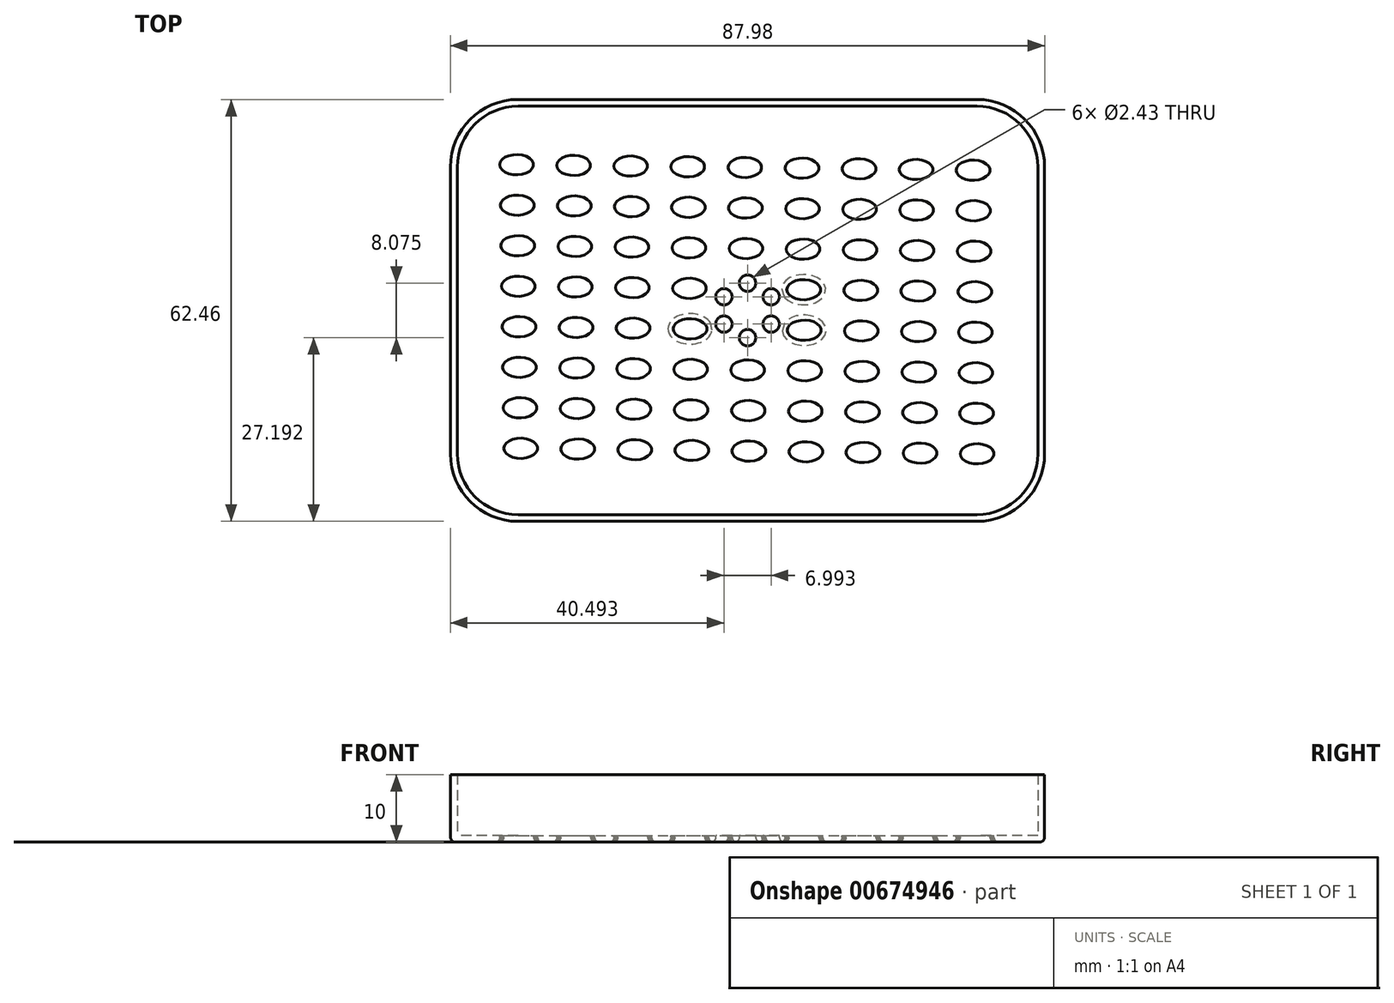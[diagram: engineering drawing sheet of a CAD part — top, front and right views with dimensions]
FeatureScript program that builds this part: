
annotation { "Feature Type Name" : "Feature", "Feature Type Description" : "" }
export const myFeature = defineFeature(function(context is Context, id is Id, definition is map)
    precondition{}
    {
        {
            var Q0;
            Q0=qCreatedBy(makeId("Top.planeOp"),FACE);
            var sketch = newSketch(context, id + "F0", { "sketchPlane" : qUnion([Q0])});
            skLineSegment(sketch, "E0.bottom", {"start": v(-33.99, 31.23) * mm, "end": v(33.99, 31.23) * mm});
            skLineSegment(sketch, "E0.top", {"start": v(-33.99, -31.23) * mm, "end": v(33.99, -31.23) * mm});
            skLineSegment(sketch, "E0.left", {"start": v(-43.99, 21.23) * mm, "end": v(-43.99, -21.23) * mm});
            skLineSegment(sketch, "E0.right", {"start": v(43.99, 21.23) * mm, "end": v(43.99, -21.23) * mm});
            skPoint(sketch, "E0.middle", {"position": v(0, 0) * mm});
            skPoint(sketch, "E1.visualSharp", {"position": v(-43.99, 31.23) * mm});
            skArc(sketch, "E1.filletArc", {"start": v(-33.99, 31.23) * mm, "mid": v(-41.06, 28.3) * mm, "end": v(-43.99, 21.23) * mm});
            skPoint(sketch, "E2.visualSharp", {"position": v(43.99, 31.23) * mm});
            skArc(sketch, "E2.filletArc", {"start": v(43.99, 21.23) * mm, "mid": v(41.06, 28.3) * mm, "end": v(33.99, 31.23) * mm});
            skPoint(sketch, "E3.visualSharp", {"position": v(43.99, -31.23) * mm});
            skArc(sketch, "E3.filletArc", {"start": v(33.99, -31.23) * mm, "mid": v(41.06, -28.3) * mm, "end": v(43.99, -21.23) * mm});
            skPoint(sketch, "E4.visualSharp", {"position": v(-43.99, -31.23) * mm});
            skArc(sketch, "E4.filletArc", {"start": v(-43.99, -21.23) * mm, "mid": v(-41.06, -28.3) * mm, "end": v(-33.99, -31.23) * mm});
            skSolve(sketch);
        }
        {
            var Q0;
            Q0 = qSketchRegion(id + "F0", true);
            extrude(context, id + "F1", {"entities" : qUnion([Q0]), "depth" : 10 * mm, "offsetDistance" : 25 * mm});
        }
        {
            var Q0;
            Q0=makeQuery(id+"F1.opExtrude","CAP_FACE",FACE,{"disambiguationData":[OSD([sQuery(id+"F0.wireOp",EDGE,"E0.bottom"),sQuery(id+"F0.wireOp",EDGE,"E0.top"),sQuery(id+"F0.wireOp",EDGE,"E0.left"),sQuery(id+"F0.wireOp",EDGE,"E0.right"),sQuery(id+"F0.wireOp",EDGE,"E1.filletArc"),sQuery(id+"F0.wireOp",EDGE,"E2.filletArc"),sQuery(id+"F0.wireOp",EDGE,"E3.filletArc"),sQuery(id+"F0.wireOp",EDGE,"E4.filletArc")])],"isStart":false});
            shell(context, id + "F2", {"entities" : qUnion([Q0]), "thickness" : 1 * mm});
        }
        {
            var Q0;
            Q0=makeQuery(id+"F2.opShell","OFFSET_FACE",FACE,{"disambiguationData":[OSD([sQuery(id+"F0.wireOp",EDGE,"E0.bottom"),sQuery(id+"F0.wireOp",EDGE,"E0.top"),sQuery(id+"F0.wireOp",EDGE,"E0.left"),sQuery(id+"F0.wireOp",EDGE,"E0.right"),sQuery(id+"F0.wireOp",EDGE,"E1.filletArc"),sQuery(id+"F0.wireOp",EDGE,"E2.filletArc"),sQuery(id+"F0.wireOp",EDGE,"E3.filletArc"),sQuery(id+"F0.wireOp",EDGE,"E4.filletArc")])]});
            var sketch = newSketch(context, id + "F3", { "sketchPlane" : qUnion([Q0])});
            skEllipse(sketch, "E5", {"center": v(33.99, -21.23) * mm, "majorRadius": 2.5 * mm, "minorRadius": 1.5 * mm, "majorAxis": v(-1, 0)});
            skEllipse(sketch, "E6.0.1.0", {"center": v(33.9, -15.23) * mm, "majorRadius": 2.5 * mm, "minorRadius": 1.5 * mm, "majorAxis": v(-1, 0)});
            skEllipse(sketch, "E6.0.2.0", {"center": v(33.82, -9.23) * mm, "majorRadius": 2.5 * mm, "minorRadius": 1.5 * mm, "majorAxis": v(-1, 0)});
            skEllipse(sketch, "E6.0.3.0", {"center": v(33.74, -3.23) * mm, "majorRadius": 2.5 * mm, "minorRadius": 1.5 * mm, "majorAxis": v(-1, 0)});
            skEllipse(sketch, "E6.0.4.0", {"center": v(33.65, 2.77) * mm, "majorRadius": 2.5 * mm, "minorRadius": 1.5 * mm, "majorAxis": v(-1, 0)});
            skEllipse(sketch, "E6.0.5.0", {"center": v(33.57, 8.76) * mm, "majorRadius": 2.5 * mm, "minorRadius": 1.5 * mm, "majorAxis": v(-1, 0)});
            skEllipse(sketch, "E6.0.6.0", {"center": v(33.48, 14.76) * mm, "majorRadius": 2.5 * mm, "minorRadius": 1.5 * mm, "majorAxis": v(-1, 0)});
            skEllipse(sketch, "E6.0.7.0", {"center": v(33.4, 20.76) * mm, "majorRadius": 2.5 * mm, "minorRadius": 1.5 * mm, "majorAxis": v(-1, 0)});
            skEllipse(sketch, "E6.1.0.0", {"center": v(25.54, -21.13) * mm, "majorRadius": 2.5 * mm, "minorRadius": 1.5 * mm, "majorAxis": v(-1, 0)});
            skEllipse(sketch, "E6.1.1.0", {"center": v(25.45, -15.13) * mm, "majorRadius": 2.5 * mm, "minorRadius": 1.5 * mm, "majorAxis": v(-1, 0)});
            skEllipse(sketch, "E6.1.2.0", {"center": v(25.37, -9.13) * mm, "majorRadius": 2.5 * mm, "minorRadius": 1.5 * mm, "majorAxis": v(-1, 0)});
            skEllipse(sketch, "E6.1.3.0", {"center": v(25.29, -3.13) * mm, "majorRadius": 2.5 * mm, "minorRadius": 1.5 * mm, "majorAxis": v(-1, 0)});
            skEllipse(sketch, "E6.1.4.0", {"center": v(25.2, 2.87) * mm, "majorRadius": 2.5 * mm, "minorRadius": 1.5 * mm, "majorAxis": v(-1, 0)});
            skEllipse(sketch, "E6.1.5.0", {"center": v(25.12, 8.87) * mm, "majorRadius": 2.5 * mm, "minorRadius": 1.5 * mm, "majorAxis": v(-1, 0)});
            skEllipse(sketch, "E6.1.6.0", {"center": v(25.03, 14.87) * mm, "majorRadius": 2.5 * mm, "minorRadius": 1.5 * mm, "majorAxis": v(-1, 0)});
            skEllipse(sketch, "E6.1.7.0", {"center": v(24.95, 20.87) * mm, "majorRadius": 2.5 * mm, "minorRadius": 1.5 * mm, "majorAxis": v(-1, 0)});
            skEllipse(sketch, "E6.2.0.0", {"center": v(17.09, -21.03) * mm, "majorRadius": 2.5 * mm, "minorRadius": 1.5 * mm, "majorAxis": v(-1, 0)});
            skEllipse(sketch, "E6.2.1.0", {"center": v(17, -15.03) * mm, "majorRadius": 2.5 * mm, "minorRadius": 1.5 * mm, "majorAxis": v(-1, 0)});
            skEllipse(sketch, "E6.2.2.0", {"center": v(16.92, -9.03) * mm, "majorRadius": 2.5 * mm, "minorRadius": 1.5 * mm, "majorAxis": v(-1, 0)});
            skEllipse(sketch, "E6.2.3.0", {"center": v(16.84, -3.03) * mm, "majorRadius": 2.5 * mm, "minorRadius": 1.5 * mm, "majorAxis": v(-1, 0)});
            skEllipse(sketch, "E6.2.4.0", {"center": v(16.75, 2.97) * mm, "majorRadius": 2.5 * mm, "minorRadius": 1.5 * mm, "majorAxis": v(-1, 0)});
            skEllipse(sketch, "E6.2.5.0", {"center": v(16.67, 8.97) * mm, "majorRadius": 2.5 * mm, "minorRadius": 1.5 * mm, "majorAxis": v(-1, 0)});
            skEllipse(sketch, "E6.2.6.0", {"center": v(16.58, 14.97) * mm, "majorRadius": 2.5 * mm, "minorRadius": 1.5 * mm, "majorAxis": v(-1, 0)});
            skEllipse(sketch, "E6.2.7.0", {"center": v(16.5, 20.97) * mm, "majorRadius": 2.5 * mm, "minorRadius": 1.5 * mm, "majorAxis": v(-1, 0)});
            skEllipse(sketch, "E6.3.0.0", {"center": v(8.64, -20.93) * mm, "majorRadius": 2.5 * mm, "minorRadius": 1.5 * mm, "majorAxis": v(-1, 0)});
            skEllipse(sketch, "E6.3.1.0", {"center": v(8.56, -14.93) * mm, "majorRadius": 2.5 * mm, "minorRadius": 1.5 * mm, "majorAxis": v(-1, 0)});
            skEllipse(sketch, "E6.3.2.0", {"center": v(8.47, -8.93) * mm, "majorRadius": 2.5 * mm, "minorRadius": 1.5 * mm, "majorAxis": v(-1, 0)});
            skEllipse(sketch, "E6.3.3.0", {"center": v(8.39, -2.93) * mm, "majorRadius": 2.5 * mm, "minorRadius": 1.5 * mm, "majorAxis": v(-1, 0)});
            skEllipse(sketch, "E6.3.4.0", {"center": v(8.3, 3.07) * mm, "majorRadius": 2.5 * mm, "minorRadius": 1.5 * mm, "majorAxis": v(-1, 0)});
            skEllipse(sketch, "E6.3.5.0", {"center": v(8.22, 9.07) * mm, "majorRadius": 2.5 * mm, "minorRadius": 1.5 * mm, "majorAxis": v(-1, 0)});
            skEllipse(sketch, "E6.3.6.0", {"center": v(8.14, 15.07) * mm, "majorRadius": 2.5 * mm, "minorRadius": 1.5 * mm, "majorAxis": v(-1, 0)});
            skEllipse(sketch, "E6.3.7.0", {"center": v(8.05, 21.07) * mm, "majorRadius": 2.5 * mm, "minorRadius": 1.5 * mm, "majorAxis": v(-1, 0)});
            skEllipse(sketch, "E6.4.0.0", {"center": v(0.19, -20.82) * mm, "majorRadius": 2.5 * mm, "minorRadius": 1.5 * mm, "majorAxis": v(-1, 0)});
            skEllipse(sketch, "E6.4.1.0", {"center": v(0.1, -14.82) * mm, "majorRadius": 2.5 * mm, "minorRadius": 1.5 * mm, "majorAxis": v(-1, 0)});
            skEllipse(sketch, "E6.4.2.0", {"center": v(0.02, -8.83) * mm, "majorRadius": 2.5 * mm, "minorRadius": 1.5 * mm, "majorAxis": v(-1, 0)});
            skEllipse(sketch, "E6.4.5.0", {"center": v(-0.23, 9.17) * mm, "majorRadius": 2.5 * mm, "minorRadius": 1.5 * mm, "majorAxis": v(-1, 0)});
            skEllipse(sketch, "E6.4.6.0", {"center": v(-0.31, 15.17) * mm, "majorRadius": 2.5 * mm, "minorRadius": 1.5 * mm, "majorAxis": v(-1, 0)});
            skEllipse(sketch, "E6.4.7.0", {"center": v(-0.4, 21.17) * mm, "majorRadius": 2.5 * mm, "minorRadius": 1.5 * mm, "majorAxis": v(-1, 0)});
            skEllipse(sketch, "E6.5.0.0", {"center": v(-8.26, -20.72) * mm, "majorRadius": 2.5 * mm, "minorRadius": 1.5 * mm, "majorAxis": v(-1, 0)});
            skEllipse(sketch, "E6.5.1.0", {"center": v(-8.34, -14.72) * mm, "majorRadius": 2.5 * mm, "minorRadius": 1.5 * mm, "majorAxis": v(-1, 0)});
            skEllipse(sketch, "E6.5.2.0", {"center": v(-8.43, -8.72) * mm, "majorRadius": 2.5 * mm, "minorRadius": 1.5 * mm, "majorAxis": v(-1, 0)});
            skEllipse(sketch, "E6.5.3.0", {"center": v(-8.51, -2.72) * mm, "majorRadius": 2.5 * mm, "minorRadius": 1.5 * mm, "majorAxis": v(-1, 0)});
            skEllipse(sketch, "E6.5.4.0", {"center": v(-8.6, 3.28) * mm, "majorRadius": 2.5 * mm, "minorRadius": 1.5 * mm, "majorAxis": v(-1, 0)});
            skEllipse(sketch, "E6.5.5.0", {"center": v(-8.68, 9.27) * mm, "majorRadius": 2.5 * mm, "minorRadius": 1.5 * mm, "majorAxis": v(-1, 0)});
            skEllipse(sketch, "E6.5.6.0", {"center": v(-8.76, 15.27) * mm, "majorRadius": 2.5 * mm, "minorRadius": 1.5 * mm, "majorAxis": v(-1, 0)});
            skEllipse(sketch, "E6.5.7.0", {"center": v(-8.85, 21.27) * mm, "majorRadius": 2.5 * mm, "minorRadius": 1.5 * mm, "majorAxis": v(-1, 0)});
            skEllipse(sketch, "E6.6.0.0", {"center": v(-16.7, -20.62) * mm, "majorRadius": 2.5 * mm, "minorRadius": 1.5 * mm, "majorAxis": v(-1, 0)});
            skEllipse(sketch, "E6.6.1.0", {"center": v(-16.8, -14.62) * mm, "majorRadius": 2.5 * mm, "minorRadius": 1.5 * mm, "majorAxis": v(-1, 0)});
            skEllipse(sketch, "E6.6.2.0", {"center": v(-16.88, -8.62) * mm, "majorRadius": 2.5 * mm, "minorRadius": 1.5 * mm, "majorAxis": v(-1, 0)});
            skEllipse(sketch, "E6.6.3.0", {"center": v(-16.96, -2.62) * mm, "majorRadius": 2.5 * mm, "minorRadius": 1.5 * mm, "majorAxis": v(-1, 0)});
            skEllipse(sketch, "E6.6.4.0", {"center": v(-17.04, 3.38) * mm, "majorRadius": 2.5 * mm, "minorRadius": 1.5 * mm, "majorAxis": v(-1, 0)});
            skEllipse(sketch, "E6.6.5.0", {"center": v(-17.13, 9.38) * mm, "majorRadius": 2.5 * mm, "minorRadius": 1.5 * mm, "majorAxis": v(-1, 0)});
            skEllipse(sketch, "E6.6.6.0", {"center": v(-17.21, 15.38) * mm, "majorRadius": 2.5 * mm, "minorRadius": 1.5 * mm, "majorAxis": v(-1, 0)});
            skEllipse(sketch, "E6.6.7.0", {"center": v(-17.3, 21.38) * mm, "majorRadius": 2.5 * mm, "minorRadius": 1.5 * mm, "majorAxis": v(-1, 0)});
            skEllipse(sketch, "E6.7.0.0", {"center": v(-25.16, -20.52) * mm, "majorRadius": 2.5 * mm, "minorRadius": 1.5 * mm, "majorAxis": v(-1, 0)});
            skEllipse(sketch, "E6.7.1.0", {"center": v(-25.24, -14.52) * mm, "majorRadius": 2.5 * mm, "minorRadius": 1.5 * mm, "majorAxis": v(-1, 0)});
            skEllipse(sketch, "E6.7.2.0", {"center": v(-25.33, -8.52) * mm, "majorRadius": 2.5 * mm, "minorRadius": 1.5 * mm, "majorAxis": v(-1, 0)});
            skEllipse(sketch, "E6.7.3.0", {"center": v(-25.41, -2.52) * mm, "majorRadius": 2.5 * mm, "minorRadius": 1.5 * mm, "majorAxis": v(-1, 0)});
            skEllipse(sketch, "E6.7.4.0", {"center": v(-25.5, 3.48) * mm, "majorRadius": 2.5 * mm, "minorRadius": 1.5 * mm, "majorAxis": v(-1, 0)});
            skEllipse(sketch, "E6.7.5.0", {"center": v(-25.58, 9.48) * mm, "majorRadius": 2.5 * mm, "minorRadius": 1.5 * mm, "majorAxis": v(-1, 0)});
            skEllipse(sketch, "E6.7.6.0", {"center": v(-25.66, 15.48) * mm, "majorRadius": 2.5 * mm, "minorRadius": 1.5 * mm, "majorAxis": v(-1, 0)});
            skEllipse(sketch, "E6.7.7.0", {"center": v(-25.75, 21.48) * mm, "majorRadius": 2.5 * mm, "minorRadius": 1.5 * mm, "majorAxis": v(-1, 0)});
            skEllipse(sketch, "E6.8.0.0", {"center": v(-33.6, -20.42) * mm, "majorRadius": 2.5 * mm, "minorRadius": 1.5 * mm, "majorAxis": v(-1, 0)});
            skEllipse(sketch, "E6.8.1.0", {"center": v(-33.7, -14.42) * mm, "majorRadius": 2.5 * mm, "minorRadius": 1.5 * mm, "majorAxis": v(-1, 0)});
            skEllipse(sketch, "E6.8.2.0", {"center": v(-33.78, -8.42) * mm, "majorRadius": 2.5 * mm, "minorRadius": 1.5 * mm, "majorAxis": v(-1, 0)});
            skEllipse(sketch, "E6.8.3.0", {"center": v(-33.86, -2.42) * mm, "majorRadius": 2.5 * mm, "minorRadius": 1.5 * mm, "majorAxis": v(-1, 0)});
            skEllipse(sketch, "E6.8.4.0", {"center": v(-33.94, 3.58) * mm, "majorRadius": 2.5 * mm, "minorRadius": 1.5 * mm, "majorAxis": v(-1, 0)});
            skEllipse(sketch, "E6.8.5.0", {"center": v(-34.03, 9.58) * mm, "majorRadius": 2.5 * mm, "minorRadius": 1.5 * mm, "majorAxis": v(-1, 0)});
            skEllipse(sketch, "E6.8.6.0", {"center": v(-34.11, 15.58) * mm, "majorRadius": 2.5 * mm, "minorRadius": 1.5 * mm, "majorAxis": v(-1, 0)});
            skEllipse(sketch, "E6.8.7.0", {"center": v(-34.2, 21.58) * mm, "majorRadius": 2.5 * mm, "minorRadius": 1.5 * mm, "majorAxis": v(-1, 0)});
            skLineSegment(sketch, "E6.direction1", {"start": v(33.99, -21.23) * mm, "end": v(25.54, -21.13) * mm, "construction": true});
            skLineSegment(sketch, "E6.direction2", {"start": v(33.99, -21.23) * mm, "end": v(33.9, -15.23) * mm, "construction": true});
            skCircle(sketch, "E7", {"center": v(0, -4.04) * mm, "radius": 1.21 * mm});
            skCircle(sketch, "E8.1.0", {"center": v(3.5, -2.02) * mm, "radius": 1.21 * mm});
            skCircle(sketch, "E8.2.0", {"center": v(3.5, 2.02) * mm, "radius": 1.21 * mm});
            skCircle(sketch, "E8.3.0", {"center": v(0, 4.04) * mm, "radius": 1.21 * mm});
            skCircle(sketch, "E8.4.0", {"center": v(-3.5, 2.02) * mm, "radius": 1.21 * mm});
            skCircle(sketch, "E8.5.0", {"center": v(-3.5, -2.02) * mm, "radius": 1.21 * mm});
            skPoint(sketch, "E8.center", {"position": v(0, 0) * mm});
            skSolve(sketch);
        }
        {
            var Q0;
            Q0 = qSketchRegion(id + "F3", true);
            extrude(context, id + "F4", {"entities" : qUnion([Q0]), "operationType" : NewBodyOperationType.REMOVE, "oppositeDirection" : true, "depth" : 25 * mm, "offsetDistance" : 25 * mm});
        }
        {
            var Q0;
            Q0=makeQuery(id+"F1.opExtrude","CAP_FACE",FACE,{"disambiguationData":[OSD([sQuery(id+"F0.wireOp",EDGE,"E0.bottom"),sQuery(id+"F0.wireOp",EDGE,"E0.top"),sQuery(id+"F0.wireOp",EDGE,"E0.left"),sQuery(id+"F0.wireOp",EDGE,"E0.right"),sQuery(id+"F0.wireOp",EDGE,"E1.filletArc"),sQuery(id+"F0.wireOp",EDGE,"E2.filletArc"),sQuery(id+"F0.wireOp",EDGE,"E3.filletArc"),sQuery(id+"F0.wireOp",EDGE,"E4.filletArc")])],"isStart":true});
            fillet(context, id + "F5", {"entities" : qUnion([Q0]), "radius" : .75 * mm, "tangentPropagation" : true, "allowEdgeOverflow" : false});
        }
    });
